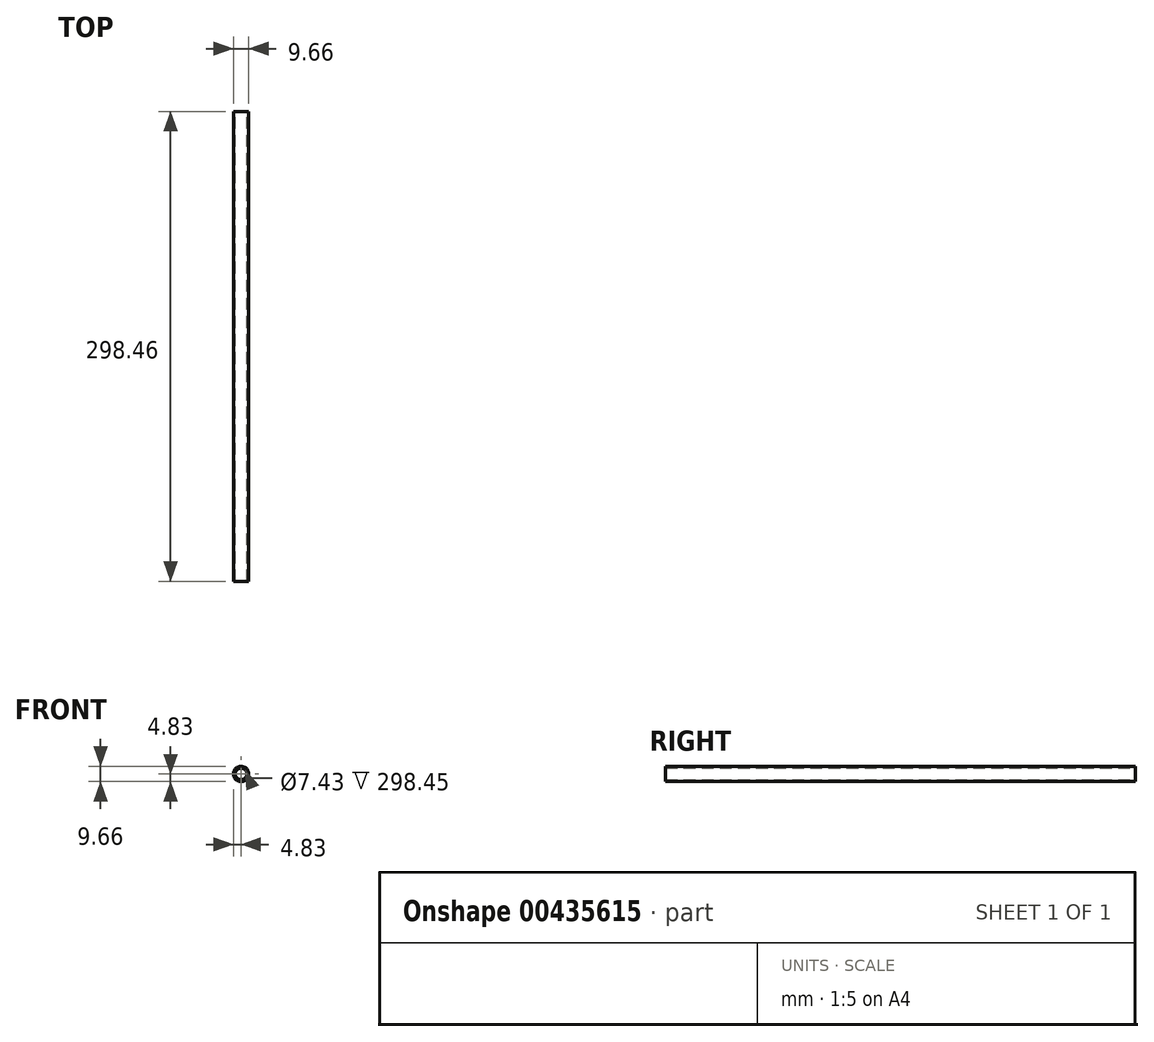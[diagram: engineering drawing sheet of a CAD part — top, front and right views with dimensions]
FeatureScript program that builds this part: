
annotation { "Feature Type Name" : "Feature", "Feature Type Description" : "" }
export const myFeature = defineFeature(function(context is Context, id is Id, definition is map)
    precondition{}
    {
        {
            var Q0;
            Q0=qCreatedBy(makeId("Front.planeOp"),FACE);
            var sketch = newSketch(context, id + "F0", { "sketchPlane" : qUnion([Q0])});
            skCircle(sketch, "E0", {"center": v(0, 0) * mm, "radius": 3.71 * mm});
            skCircle(sketch, "E1", {"center": v(0, 0) * mm, "radius": 4.83 * mm});
            skSolve(sketch);
        }
        {
            var Q0;
            Q0=makeQuery(id+"F0.imprint","IMPRINT",FACE,{"disambiguationData":[TD([[makeQuery(id+"F0.imprint","IMPRINT",EDGE,{"derivedFrom":sQuery(id+"F0.wireOp",EDGE,"E0")}),-1.0]])]});
            extrude(context, id + "F1", {"entities" : qUnion([Q0]), "depth" : 298.45 * mm, "offsetDistance" : 25.4 * mm, "symmetric" : true});
        }
    });
